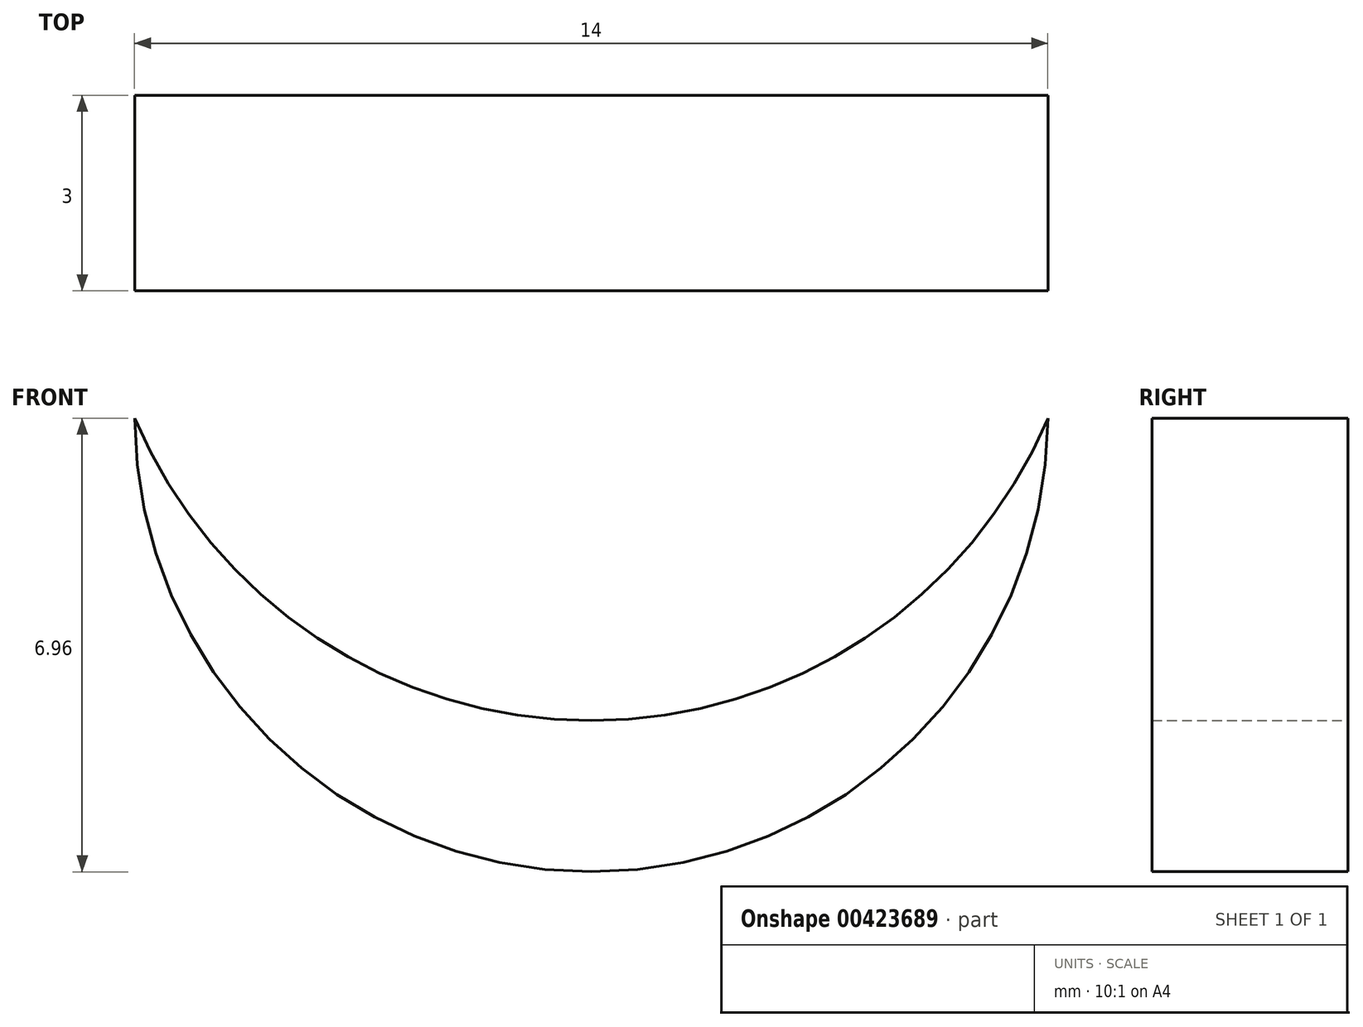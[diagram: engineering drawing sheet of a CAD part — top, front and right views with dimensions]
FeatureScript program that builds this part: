
annotation { "Feature Type Name" : "Feature", "Feature Type Description" : "" }
export const myFeature = defineFeature(function(context is Context, id is Id, definition is map)
    precondition{}
    {
        {
            var Q0;
            Q0=qCreatedBy(makeId("Front.planeOp"),FACE);
            var sketch = newSketch(context, id + "F0", { "sketchPlane" : qUnion([Q0])});
            skArc(sketch, "E0", {"start": v(-19.85, 0) * mm, "mid": v(-12.85, -6.96) * mm, "end": v(-5.85, 0) * mm});
            skArc(sketch, "E1", {"start": v(-19.85, 0) * mm, "mid": v(-12.85, -4.64) * mm, "end": v(-5.85, 0) * mm});
            skSolve(sketch);
        }
        {
            var Q0;
            Q0=makeQuery(id+"F0.imprint","IMPRINT",FACE,{"disambiguationData":[TD([[makeQuery(id+"F0.imprint","IMPRINT",EDGE,{"derivedFrom":sQuery(id+"F0.wireOp",EDGE,"E0")}),-1.0]])]});
            var Q1;
            Q1=makeQuery(id+"F0.imprint","IMPRINT",FACE,{"disambiguationData":[TD([[makeQuery(id+"F0.imprint","IMPRINT",EDGE,{"derivedFrom":sQuery(id+"F0.wireOp",EDGE,"E0")}),1.0]])]});
            extrude(context, id + "F1", {"entities" : qUnion([Q0, Q1]), "depth" : 3 * mm});
        }
    });
